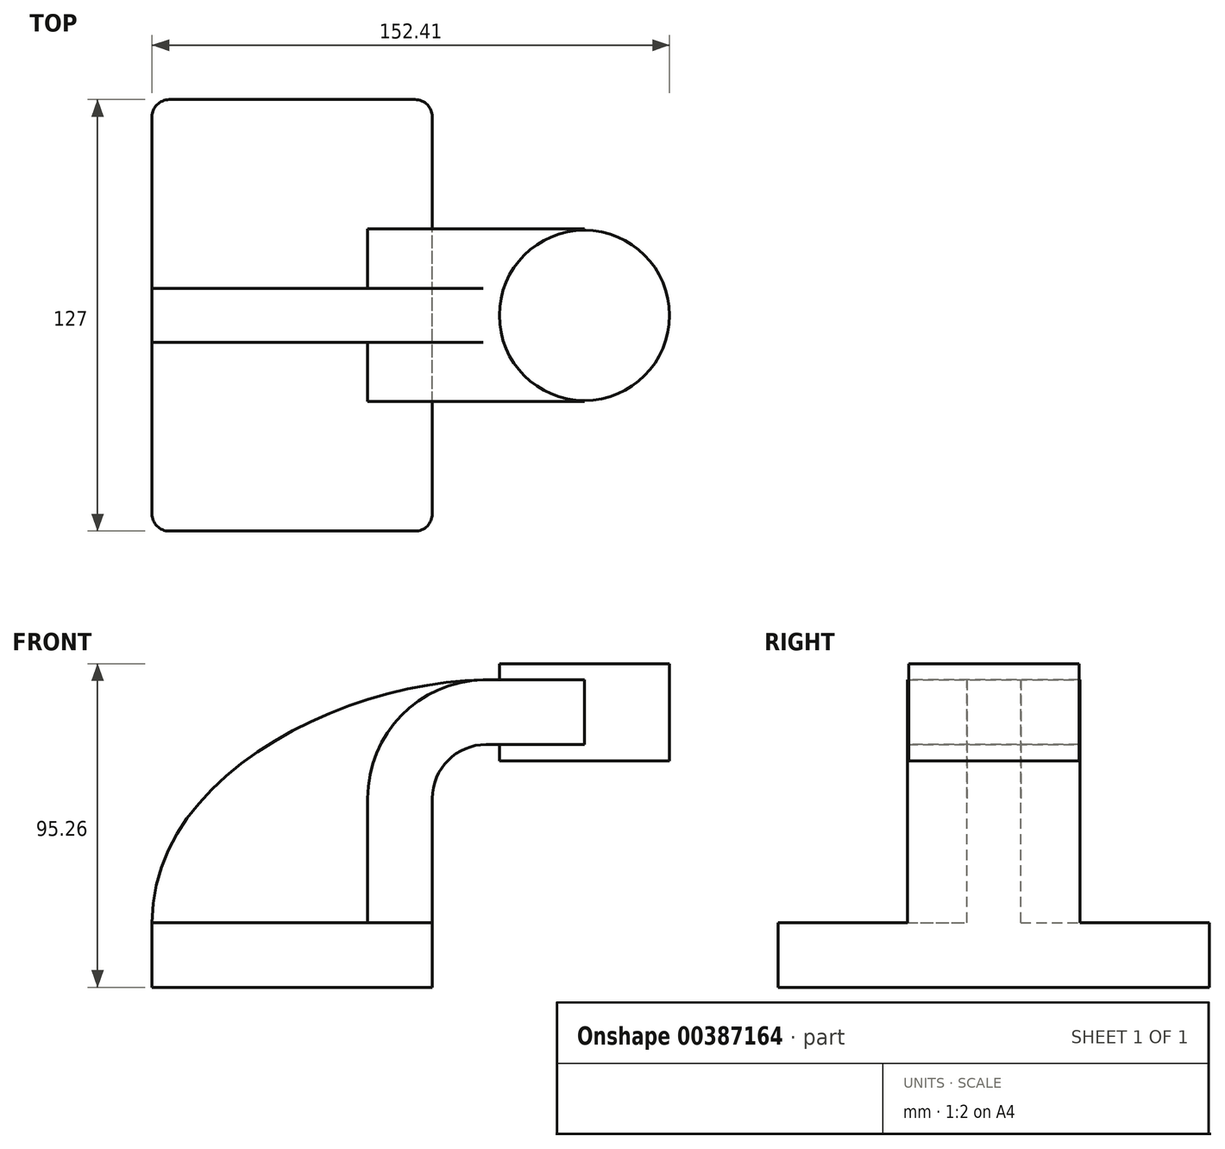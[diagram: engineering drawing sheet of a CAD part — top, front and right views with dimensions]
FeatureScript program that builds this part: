
annotation { "Feature Type Name" : "Feature", "Feature Type Description" : "" }
export const myFeature = defineFeature(function(context is Context, id is Id, definition is map)
    precondition{}
    {
        {
            var Q0;
            Q0=qCreatedBy(makeId("Front.planeOp"),FACE);
            var sketch = newSketch(context, id + "F0", { "sketchPlane" : qUnion([Q0])});
            skLineSegment(sketch, "E0.bottom", {"start": v(-41.27, 9.52) * mm, "end": v(41.27, 9.52) * mm});
            skLineSegment(sketch, "E0.top", {"start": v(-41.27, -9.53) * mm, "end": v(41.28, -9.53) * mm});
            skLineSegment(sketch, "E0.left", {"start": v(-41.27, 9.52) * mm, "end": v(-41.27, -9.53) * mm});
            skLineSegment(sketch, "E0.right", {"start": v(41.27, 9.52) * mm, "end": v(41.27, -9.52) * mm});
            skPoint(sketch, "E0.middle", {"position": v(0, 0) * mm});
            skLineSegment(sketch, "E1.bottom", {"start": v(111.12, 85.73) * mm, "end": v(60.33, 85.73) * mm});
            skLineSegment(sketch, "E1.top", {"start": v(111.13, 57.15) * mm, "end": v(60.33, 57.15) * mm});
            skLineSegment(sketch, "E1.left", {"start": v(111.12, 85.73) * mm, "end": v(111.13, 57.15) * mm});
            skLineSegment(sketch, "E1.right", {"start": v(60.33, 85.72) * mm, "end": v(60.33, 57.15) * mm});
            skPoint(sketch, "E1.middle", {"position": v(85.73, 71.44) * mm});
            skLineSegment(sketch, "E2", {"start": v(41.27, 9.52) * mm, "end": v(41.27, 46.05) * mm});
            skArc(sketch, "E3", {"start": v(41.28, 46.05) * mm, "mid": v(45.92, 57.28) * mm, "end": v(57.15, 61.93) * mm});
            skLineSegment(sketch, "E4", {"start": v(57.15, 61.93) * mm, "end": v(86.06, 61.93) * mm});
            skLineSegment(sketch, "E5.0", {"start": v(57.15, 80.98) * mm, "end": v(86.06, 80.98) * mm});
            skArc(sketch, "E5.1", {"start": v(22.23, 46.05) * mm, "mid": v(32.45, 70.75) * mm, "end": v(57.15, 80.98) * mm});
            skLineSegment(sketch, "E5.2", {"start": v(22.22, 9.52) * mm, "end": v(22.22, 46.05) * mm});
            skLineSegment(sketch, "E6", {"start": v(86.06, 85.73) * mm, "end": v(86.06, 57.15) * mm});
            skPoint(sketch, "E6.startSnap0", {"position": v(85.73, 85.73) * mm});
            skFitSpline(sketch, "E7", {"points": [v(-41.28, 9.53) * mm, v(57.15, 80.98) * mm], "startDerivative": vector(-0.19, 132.3) * mm, "endDerivative": vector(121.7, 0.97) * mm});
            skSolve(sketch);
        }
        {
            var Q0;
            Q0=makeQuery(id+"F0.imprint","IMPRINT",FACE,{"disambiguationData":[TD([[makeQuery(id+"F0.imprint","IMPRINT",EDGE,{"derivedFrom":sQuery(id+"F0.wireOp",EDGE,"E0.top")}),1.0]])]});
            extrude(context, id + "F1", {"entities" : qUnion([Q0]), "depth" : 127 * mm, "symmetric" : true});
        }
        {
            var Q0;
            {var subQ1=sQuery(id+"F0.wireOp",EDGE,"E2");Q0=makeQuery(id+"F0.imprint","IMPRINT",FACE,{"disambiguationData":[TD([[makeQuery(id+"F0.imprint","IMPRINT",EDGE,{"derivedFrom":subQ1}),1.0]])]});}
            var Q1;
            {var subQ0=sQuery(id+"F0.wireOp",EDGE,"E5.0");var subQ1=sQuery(id+"F0.wireOp",EDGE,"E1.right");var subQ2=makeQuery(id+"F0.imprint","INTERSECT",VERTEX,{"derivedFrom":[subQ1,subQ0]});Q1=makeQuery(id+"F0.imprint","IMPRINT",FACE,{"disambiguationData":[TD([[makeQuery(id+"F0.imprint","IMPRINT",EDGE,{"disambiguationData":[TD([[subQ2,-1.0]])],"derivedFrom":subQ1}),1.0]])]});}
            extrude(context, id + "F2", {"entities" : qUnion([Q0, Q1]), "operationType" : NewBodyOperationType.ADD, "depth" : 50.8 * mm, "symmetric" : true});
        }
        {
            var Q0;
            {var subQ1=sQuery(id+"F0.wireOp",EDGE,"E2");Q0=makeQuery(id+"F0.imprint","IMPRINT",FACE,{"disambiguationData":[TD([[makeQuery(id+"F0.imprint","IMPRINT",EDGE,{"derivedFrom":subQ1}),1.0]])]});}
            var Q1;
            {var subQ0=sQuery(id+"F0.wireOp",EDGE,"E5.0");var subQ1=sQuery(id+"F0.wireOp",EDGE,"E1.right");var subQ2=makeQuery(id+"F0.imprint","INTERSECT",VERTEX,{"derivedFrom":[subQ1,subQ0]});Q1=makeQuery(id+"F0.imprint","IMPRINT",FACE,{"disambiguationData":[TD([[makeQuery(id+"F0.imprint","IMPRINT",EDGE,{"disambiguationData":[TD([[subQ2,-1.0]])],"derivedFrom":subQ1}),1.0]])]});}
            extrude(context, id + "F3", {"entities" : qUnion([Q0, Q1]), "operationType" : NewBodyOperationType.ADD, "depth" : 50.8 * mm, "symmetric" : true});
        }
        {
            var Q0;
            {var subQ3=sQuery(id+"F0.wireOp",EDGE,"E5.2");Q0=makeQuery(id+"F0.imprint","IMPRINT",FACE,{"disambiguationData":[TD([[makeQuery(id+"F0.imprint","IMPRINT",EDGE,{"derivedFrom":subQ3}),1.0]])]});}
            extrude(context, id + "F4", {"entities" : qUnion([Q0]), "operationType" : NewBodyOperationType.ADD, "depth" : 15.88 * mm, "symmetric" : true});
        }
        {
            var Q0;
            {var subQ0=sQuery(id+"F0.wireOp",EDGE,"E1.left");Q0=makeQuery(id+"F0.imprint","IMPRINT",FACE,{"disambiguationData":[TD([[makeQuery(id+"F0.imprint","IMPRINT",EDGE,{"derivedFrom":subQ0}),-1.0]])]});}
            var Q1;
            Q1=sQuery(id+"F0.wireOp",EDGE,"E6");
            revolve(context, id + "F5", {"operationType" : NewBodyOperationType.ADD, "entities" : qUnion([Q0]), "axis" : qUnion([Q1]), "revolveType" : RevolveType.FULL});
        }
        {
            var Q0;
            Q0=makeQuery(id+"F1.opExtrude","CAP_EDGE",EDGE,{"disambiguationData":[OSD([sQuery(id+"F0.wireOp",EDGE,"E0.left")])],"isStart":true});
            var Q1;
            Q1=makeQuery(id+"F1.opExtrude","CAP_EDGE",EDGE,{"disambiguationData":[OSD([sQuery(id+"F0.wireOp",EDGE,"E0.left")])],"isStart":false});
            var Q2;
            Q2=makeQuery(id+"F1.opExtrude","CAP_EDGE",EDGE,{"disambiguationData":[OSD([sQuery(id+"F0.wireOp",EDGE,"E0.right")])],"isStart":true});
            var Q3;
            Q3=makeQuery(id+"F1.opExtrude","CAP_EDGE",EDGE,{"disambiguationData":[OSD([sQuery(id+"F0.wireOp",EDGE,"E0.right")])],"isStart":false});
            fillet(context, id + "F6", {"entities" : qUnion([Q0, Q1, Q2, Q3]), "radius" : 5.08 * mm, "tangentPropagation" : true, "allowEdgeOverflow" : false});
        }
    });
